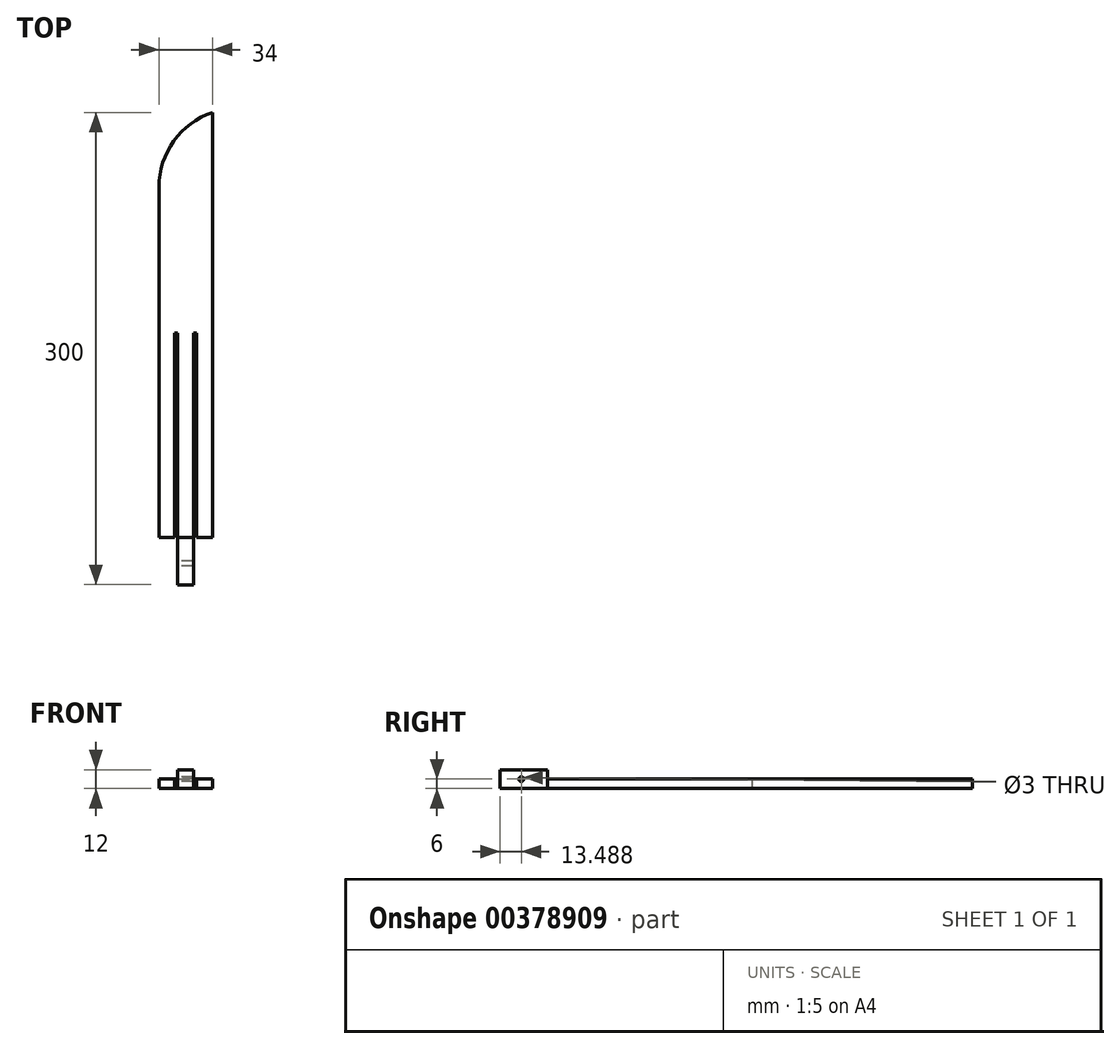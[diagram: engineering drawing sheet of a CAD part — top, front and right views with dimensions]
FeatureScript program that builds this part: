
annotation { "Feature Type Name" : "Feature", "Feature Type Description" : "" }
export const myFeature = defineFeature(function(context is Context, id is Id, definition is map)
    precondition{}
    {
        {
            var Q0;
            Q0=qCreatedBy(makeId("Top.planeOp"),FACE);
            var sketch = newSketch(context, id + "F0", { "sketchPlane" : qUnion([Q0])});
            skLineSegment(sketch, "E0.bottom", {"start": v(-19.09, 227.5) * mm, "end": v(14.91, 227.5) * mm});
            skLineSegment(sketch, "E0.left", {"start": v(-19.09, 227.5) * mm, "end": v(-19.09, -42.5) * mm});
            skLineSegment(sketch, "E0.right", {"start": v(14.91, 227.5) * mm, "end": v(14.91, -42.5) * mm});
            skLineSegment(sketch, "E1.top", {"start": v(-9.09, 87.5) * mm, "end": v(-7.09, 87.5) * mm});
            skLineSegment(sketch, "E1.left", {"start": v(-9.09, -42.5) * mm, "end": v(-9.09, 87.5) * mm});
            skLineSegment(sketch, "E1.right", {"start": v(-7.09, -72.5) * mm, "end": v(-7.09, 87.5) * mm});
            skLineSegment(sketch, "E2.top", {"start": v(2.91, 87.5) * mm, "end": v(4.91, 87.5) * mm});
            skLineSegment(sketch, "E2.left", {"start": v(2.91, -72.5) * mm, "end": v(2.91, 87.5) * mm});
            skLineSegment(sketch, "E2.right", {"start": v(4.91, -42.5) * mm, "end": v(4.91, 87.5) * mm});
            skLineSegment(sketch, "E3.trimOffspring", {"start": v(-7.09, -72.5) * mm, "end": v(2.91, -72.5) * mm});
            skLineSegment(sketch, "E4.top", {"start": v(-19.09, -42.5) * mm, "end": v(-9.09, -42.5) * mm});
            skLineSegment(sketch, "E5.top", {"start": v(4.91, -42.5) * mm, "end": v(14.91, -42.5) * mm});
            skSolve(sketch);
        }
        {
            var Q0;
            Q0=makeQuery(id+"F0.imprint","IMPRINT",FACE,{"disambiguationData":[TD([[makeQuery(id+"F0.imprint","IMPRINT",EDGE,{"derivedFrom":sQuery(id+"F0.wireOp",EDGE,"E0.bottom")}),-1.0]])]});
            extrude(context, id + "F1", {"entities" : qUnion([Q0]), "depth" : 6 * mm});
        }
        {
            var Q0;
            Q0=makeQuery(id+"F1.opExtrude","SWEPT_EDGE",EDGE,{"disambiguationData":[OSD([sQuery(id+"F0.wireOp",EDGE,"E0.bottom"),sQuery(id+"F0.wireOp",EDGE,"E0.left")])]});
            fillet(context, id + "F2", {"entities" : qUnion([Q0]), "radius" : 50 * mm, "tangentPropagation" : true, "allowEdgeOverflow" : false});
        }
        {
            var Q0;
            Q0=makeQuery(id+"F1.opExtrude","CAP_FACE",FACE,{"disambiguationData":[OSD([sQuery(id+"F0.wireOp",EDGE,"E0.bottom"),sQuery(id+"F0.wireOp",EDGE,"E0.left"),sQuery(id+"F0.wireOp",EDGE,"E0.right"),sQuery(id+"F0.wireOp",EDGE,"E1.top"),sQuery(id+"F0.wireOp",EDGE,"E1.left"),sQuery(id+"F0.wireOp",EDGE,"E1.right"),sQuery(id+"F0.wireOp",EDGE,"E2.top"),sQuery(id+"F0.wireOp",EDGE,"E2.left"),sQuery(id+"F0.wireOp",EDGE,"E2.right"),sQuery(id+"F0.wireOp",EDGE,"E3.trimOffspring"),sQuery(id+"F0.wireOp",EDGE,"E4.top"),sQuery(id+"F0.wireOp",EDGE,"E5.top")])],"isStart":false});
            var sketch = newSketch(context, id + "F3", { "sketchPlane" : qUnion([Q0])});
            skLineSegment(sketch, "E6.bottom", {"start": v(-7.09, -42.5) * mm, "end": v(2.91, -42.5) * mm});
            skLineSegment(sketch, "E6.top", {"start": v(-7.09, -72.5) * mm, "end": v(2.91, -72.5) * mm});
            skLineSegment(sketch, "E6.left", {"start": v(-7.09, -42.5) * mm, "end": v(-7.09, -72.5) * mm});
            skLineSegment(sketch, "E6.right", {"start": v(2.91, -42.5) * mm, "end": v(2.91, -72.5) * mm});
            skSolve(sketch);
        }
        {
            var Q0;
            Q0=qSketchRegion(id+"F3",true);
            extrude(context, id + "F4", {"entities" : qUnion([Q0]), "operationType" : NewBodyOperationType.ADD, "depth" : 6 * mm});
        }
        {
            var Q0;
            Q0=makeQuery(id+"F4.boolean.opBoolean","MERGE",FACE,{"derivedFrom":[makeQuery(id+"F1.opExtrude","SWEPT_FACE",FACE,{"disambiguationData":[OSD([sQuery(id+"F0.wireOp",EDGE,"E1.right")])]}),makeQuery(id+"F4.opExtrude","SWEPT_FACE",FACE,{"disambiguationData":[OSD([sQuery(id+"F3.wireOp",EDGE,"E6.left")])]})]});
            var sketch = newSketch(context, id + "F5", { "sketchPlane" : qUnion([Q0])});
            skCircle(sketch, "E7", {"center": v(59, 6) * mm, "radius": 1.5 * mm});
            skPoint(sketch, "E7.centerSnap0", {"position": v(72.5, 6) * mm});
            skSolve(sketch);
        }
        {
            var Q0;
            Q0=makeQuery(id+"F5.imprint","IMPRINT",FACE,{"disambiguationData":[TD([[makeQuery(id+"F5.imprint","IMPRINT",EDGE,{"derivedFrom":sQuery(id+"F5.wireOp",EDGE,"E7")}),1.0]])]});
            extrude(context, id + "F6", {"entities" : qUnion([Q0]), "operationType" : NewBodyOperationType.REMOVE, "endBound" : BoundingType.UP_TO_NEXT, "oppositeDirection" : true, "depth" : 25 * mm});
        }
    });
